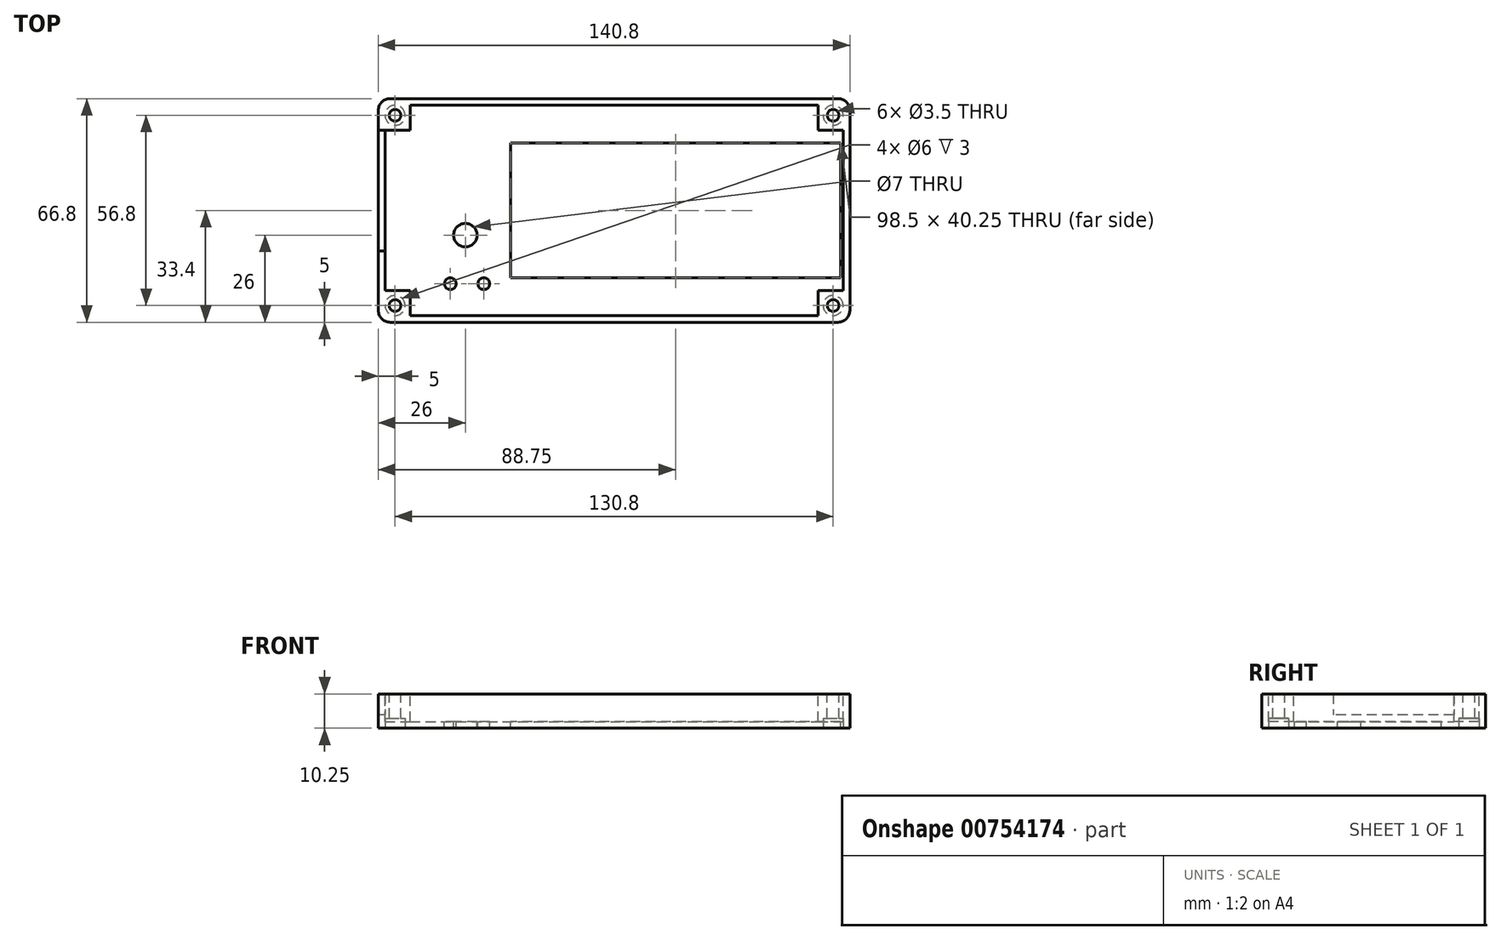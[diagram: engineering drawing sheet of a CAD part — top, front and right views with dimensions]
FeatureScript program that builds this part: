
annotation { "Feature Type Name" : "Feature", "Feature Type Description" : "" }
export const myFeature = defineFeature(function(context is Context, id is Id, definition is map)
    precondition{}
    {
        {
            var Q0;
            Q0=qCreatedBy(makeId("Top.planeOp"),FACE);
            var sketch = newSketch(context, id + "F0", { "sketchPlane" : qUnion([Q0])});
            skLineSegment(sketch, "E0.bottom", {"start": v(0, 0) * mm, "end": v(140.8, 0) * mm});
            skLineSegment(sketch, "E0.top", {"start": v(0, 66.8) * mm, "end": v(140.8, 66.8) * mm});
            skLineSegment(sketch, "E0.left", {"start": v(0, 0) * mm, "end": v(0, 66.8) * mm});
            skLineSegment(sketch, "E0.right", {"start": v(140.8, 0) * mm, "end": v(140.8, 66.8) * mm});
            skLineSegment(sketch, "E1.0", {"start": v(2, 64.8) * mm, "end": v(138.8, 64.8) * mm});
            skLineSegment(sketch, "E1.1", {"start": v(2, 2) * mm, "end": v(2, 64.8) * mm});
            skLineSegment(sketch, "E1.2", {"start": v(2, 2) * mm, "end": v(138.8, 2) * mm});
            skLineSegment(sketch, "E1.3", {"start": v(138.8, 2) * mm, "end": v(138.8, 64.8) * mm});
            skLineSegment(sketch, "E2", {"start": v(2, 57.3) * mm, "end": v(138.8, 57.3) * mm});
            skLineSegment(sketch, "E3", {"start": v(2, 9.5) * mm, "end": v(138.8, 9.5) * mm});
            skLineSegment(sketch, "E4", {"start": v(131.3, 64.8) * mm, "end": v(131.3, 2) * mm});
            skLineSegment(sketch, "E5", {"start": v(9.5, 64.8) * mm, "end": v(9.5, 2) * mm});
            skLineSegment(sketch, "E6.bottom", {"start": v(138, 53.53) * mm, "end": v(39.5, 53.53) * mm});
            skLineSegment(sketch, "E6.top", {"start": v(138, 13.28) * mm, "end": v(39.5, 13.28) * mm});
            skLineSegment(sketch, "E6.left", {"start": v(138, 53.53) * mm, "end": v(138, 13.28) * mm});
            skLineSegment(sketch, "E6.right", {"start": v(39.5, 53.53) * mm, "end": v(39.5, 13.28) * mm});
            skLineSegment(sketch, "E7", {"start": v(0, 33.4) * mm, "end": v(140.8, 33.4) * mm, "construction": true});
            skLineSegment(sketch, "E8", {"start": v(5, 83.26) * mm, "end": v(5, -9.4) * mm, "construction": true});
            skLineSegment(sketch, "E9", {"start": v(135.8, 85.49) * mm, "end": v(135.8, -7.35) * mm, "construction": true});
            skLineSegment(sketch, "E10", {"start": v(-12.85, 61.8) * mm, "end": v(160.3, 61.8) * mm, "construction": true});
            skLineSegment(sketch, "E11", {"start": v(-16.1, 5) * mm, "end": v(171.8, 5) * mm, "construction": true});
            skCircle(sketch, "E12", {"center": v(5, 61.8) * mm, "radius": 1.75 * mm});
            skCircle(sketch, "E13", {"center": v(135.8, 61.8) * mm, "radius": 1.75 * mm});
            skCircle(sketch, "E14", {"center": v(135.8, 5) * mm, "radius": 1.75 * mm});
            skCircle(sketch, "E15", {"center": v(5, 5) * mm, "radius": 1.75 * mm});
            skCircle(sketch, "E16", {"center": v(26, 26) * mm, "radius": 3.5 * mm});
            skCircle(sketch, "E17", {"center": v(21.5, 11.5) * mm, "radius": 1.75 * mm});
            skCircle(sketch, "E18", {"center": v(31.5, 11.5) * mm, "radius": 1.75 * mm});
            skSolve(sketch);
        }
        {
            var Q0;
            Q0 = qSketchRegion(id + "F0", true);
            var Q1;
            {var subQ5=sQuery(id+"F0.wireOp",EDGE,"E6.right");Q1=makeQuery(id+"F0.imprint","IMPRINT",FACE,{"disambiguationData":[TD([[makeQuery(id+"F0.imprint","IMPRINT",EDGE,{"derivedFrom":subQ5}),-1.0]])]});}
            var Q2;
            {var subQ0=sQuery(id+"F0.wireOp",EDGE,"E2");var subQ1=sQuery(id+"F0.wireOp",EDGE,"E1.1");var subQ2=makeQuery(id+"F0.imprint","INTERSECT",VERTEX,{"derivedFrom":[subQ1,subQ0]});Q2=makeQuery(id+"F0.imprint","IMPRINT",FACE,{"disambiguationData":[TD([[makeQuery(id+"F0.imprint","IMPRINT",EDGE,{"disambiguationData":[TD([[subQ2,1.0]])],"derivedFrom":subQ1}),-1.0]])]});}
            var Q3;
            Q3=makeQuery(id+"F0.imprint","IMPRINT",FACE,{"disambiguationData":[TD([[makeQuery(id+"F0.imprint","IMPRINT",EDGE,{"derivedFrom":sQuery(id+"F0.wireOp",EDGE,"E12")}),-1.0]])]});
            var Q4;
            {var subQ0=sQuery(id+"F0.wireOp",EDGE,"E4");var subQ1=sQuery(id+"F0.wireOp",EDGE,"E1.0");var subQ2=makeQuery(id+"F0.imprint","INTERSECT",VERTEX,{"derivedFrom":[subQ1,subQ0]});Q4=makeQuery(id+"F0.imprint","IMPRINT",FACE,{"disambiguationData":[TD([[makeQuery(id+"F0.imprint","IMPRINT",EDGE,{"disambiguationData":[TD([[subQ2,1.0]])],"derivedFrom":subQ1}),-1.0]])]});}
            var Q5;
            Q5=makeQuery(id+"F0.imprint","IMPRINT",FACE,{"disambiguationData":[TD([[makeQuery(id+"F0.imprint","IMPRINT",EDGE,{"derivedFrom":sQuery(id+"F0.wireOp",EDGE,"E13")}),-1.0]])]});
            var Q6;
            {var subQ5=sQuery(id+"F0.wireOp",EDGE,"E6.left");Q6=makeQuery(id+"F0.imprint","IMPRINT",FACE,{"disambiguationData":[TD([[makeQuery(id+"F0.imprint","IMPRINT",EDGE,{"derivedFrom":subQ5}),1.0]])]});}
            var Q7;
            Q7=makeQuery(id+"F0.imprint","IMPRINT",FACE,{"disambiguationData":[TD([[makeQuery(id+"F0.imprint","IMPRINT",EDGE,{"derivedFrom":sQuery(id+"F0.wireOp",EDGE,"E14")}),-1.0]])]});
            var Q8;
            {var subQ0=sQuery(id+"F0.wireOp",EDGE,"E4");var subQ1=sQuery(id+"F0.wireOp",EDGE,"E1.2");var subQ2=makeQuery(id+"F0.imprint","INTERSECT",VERTEX,{"derivedFrom":[subQ1,subQ0]});Q8=makeQuery(id+"F0.imprint","IMPRINT",FACE,{"disambiguationData":[TD([[makeQuery(id+"F0.imprint","IMPRINT",EDGE,{"disambiguationData":[TD([[subQ2,1.0]])],"derivedFrom":subQ1}),1.0]])]});}
            var Q9;
            Q9=makeQuery(id+"F0.imprint","IMPRINT",FACE,{"disambiguationData":[TD([[makeQuery(id+"F0.imprint","IMPRINT",EDGE,{"derivedFrom":sQuery(id+"F0.wireOp",EDGE,"E15")}),-1.0]])]});
            extrude(context, id + "F1", {"entities" : qUnion([Q0, Q1, Q2, Q3, Q4, Q5, Q6, Q7, Q8, Q9]), "oppositeDirection" : true, "depth" : (6.5 + 3.75) * mm, "offsetDistance" : 25 * mm});
        }
        {
            var Q0;
            {var subQ0=sQuery(id+"F0.wireOp",EDGE,"E4");var subQ1=sQuery(id+"F0.wireOp",EDGE,"E1.0");var subQ2=makeQuery(id+"F0.imprint","INTERSECT",VERTEX,{"derivedFrom":[subQ1,subQ0]});Q0=makeQuery(id+"F0.imprint","IMPRINT",FACE,{"disambiguationData":[TD([[makeQuery(id+"F0.imprint","IMPRINT",EDGE,{"disambiguationData":[TD([[subQ2,1.0]])],"derivedFrom":subQ1}),-1.0]])]});}
            var Q1;
            {var subQ5=sQuery(id+"F0.wireOp",EDGE,"E6.right");Q1=makeQuery(id+"F0.imprint","IMPRINT",FACE,{"disambiguationData":[TD([[makeQuery(id+"F0.imprint","IMPRINT",EDGE,{"derivedFrom":subQ5}),-1.0]])]});}
            var Q2;
            {var subQ0=sQuery(id+"F0.wireOp",EDGE,"E4");var subQ1=sQuery(id+"F0.wireOp",EDGE,"E1.2");var subQ2=makeQuery(id+"F0.imprint","INTERSECT",VERTEX,{"derivedFrom":[subQ1,subQ0]});Q2=makeQuery(id+"F0.imprint","IMPRINT",FACE,{"disambiguationData":[TD([[makeQuery(id+"F0.imprint","IMPRINT",EDGE,{"disambiguationData":[TD([[subQ2,1.0]])],"derivedFrom":subQ1}),1.0]])]});}
            var Q3;
            {var subQ0=sQuery(id+"F0.wireOp",EDGE,"E2");var subQ1=sQuery(id+"F0.wireOp",EDGE,"E1.1");var subQ2=makeQuery(id+"F0.imprint","INTERSECT",VERTEX,{"derivedFrom":[subQ1,subQ0]});Q3=makeQuery(id+"F0.imprint","IMPRINT",FACE,{"disambiguationData":[TD([[makeQuery(id+"F0.imprint","IMPRINT",EDGE,{"disambiguationData":[TD([[subQ2,1.0]])],"derivedFrom":subQ1}),-1.0]])]});}
            var Q4;
            {var subQ5=sQuery(id+"F0.wireOp",EDGE,"E6.left");Q4=makeQuery(id+"F0.imprint","IMPRINT",FACE,{"disambiguationData":[TD([[makeQuery(id+"F0.imprint","IMPRINT",EDGE,{"derivedFrom":subQ5}),1.0]])]});}
            extrude(context, id + "F2", {"entities" : qUnion([Q0, Q1, Q2, Q3, Q4]), "operationType" : NewBodyOperationType.REMOVE, "oppositeDirection" : true, "depth" : 8.25 * mm, "offsetDistance" : 25 * mm});
        }
        {
            var Q0;
            Q0=makeQuery(id+"F1.opExtrude","SWEPT_EDGE",EDGE,{"disambiguationData":[OSD([sQuery(id+"F0.wireOp",EDGE,"E0.top"),sQuery(id+"F0.wireOp",EDGE,"E0.right")])]});
            var Q1;
            Q1=makeQuery(id+"F1.opExtrude","SWEPT_EDGE",EDGE,{"disambiguationData":[OSD([sQuery(id+"F0.wireOp",EDGE,"E0.top"),sQuery(id+"F0.wireOp",EDGE,"E0.left")])]});
            var Q2;
            Q2=makeQuery(id+"F1.opExtrude","SWEPT_EDGE",EDGE,{"disambiguationData":[OSD([sQuery(id+"F0.wireOp",EDGE,"E0.bottom"),sQuery(id+"F0.wireOp",EDGE,"E0.left")])]});
            var Q3;
            Q3=makeQuery(id+"F1.opExtrude","SWEPT_EDGE",EDGE,{"disambiguationData":[OSD([sQuery(id+"F0.wireOp",EDGE,"E0.bottom"),sQuery(id+"F0.wireOp",EDGE,"E0.right")])]});
            fillet(context, id + "F3", {"entities" : qUnion([Q0, Q1, Q2, Q3]), "radius" : 3.5 * mm, "tangentPropagation" : true, "allowEdgeOverflow" : false});
        }
        {
            var Q0;
            Q0=makeQuery(id+"F1.opExtrude","CAP_FACE",FACE,{"disambiguationData":[OSD([sQuery(id+"F0.wireOp",EDGE,"E0.bottom"),sQuery(id+"F0.wireOp",EDGE,"E0.top"),sQuery(id+"F0.wireOp",EDGE,"E0.left"),sQuery(id+"F0.wireOp",EDGE,"E0.right"),sQuery(id+"F0.wireOp",EDGE,"E6.bottom"),sQuery(id+"F0.wireOp",EDGE,"E6.top"),sQuery(id+"F0.wireOp",EDGE,"E6.left"),sQuery(id+"F0.wireOp",EDGE,"E6.right"),sQuery(id+"F0.wireOp",EDGE,"E12"),sQuery(id+"F0.wireOp",EDGE,"E13"),sQuery(id+"F0.wireOp",EDGE,"E14"),sQuery(id+"F0.wireOp",EDGE,"E15"),sQuery(id+"F0.wireOp",EDGE,"E16"),sQuery(id+"F0.wireOp",EDGE,"E17"),sQuery(id+"F0.wireOp",EDGE,"E18")])],"isStart":false});
            var sketch = newSketch(context, id + "F4", { "sketchPlane" : qUnion([Q0])});
            skCircle(sketch, "E19.0", {"center": v(5, -5) * mm, "radius": 3 * mm});
            skCircle(sketch, "E20.0", {"center": v(135.8, -5) * mm, "radius": 3 * mm});
            skCircle(sketch, "E21.0", {"center": v(135.8, -61.8) * mm, "radius": 3 * mm});
            skCircle(sketch, "E22.0", {"center": v(5, -61.8) * mm, "radius": 3 * mm});
            skSolve(sketch);
        }
        {
            var Q0;
            Q0 = qSketchRegion(id + "F4", true);
            extrude(context, id + "F5", {"entities" : qUnion([Q0]), "operationType" : NewBodyOperationType.REMOVE, "oppositeDirection" : true, "depth" : 3 * mm, "offsetDistance" : 25 * mm});
        }
        {
            var Q0;
            Q0=makeQuery(id+"F1.opExtrude","SWEPT_FACE",FACE,{"disambiguationData":[OSD([sQuery(id+"F0.wireOp",EDGE,"E0.left")])]});
            var sketch = newSketch(context, id + "F6", { "sketchPlane" : qUnion([Q0])});
            skLineSegment(sketch, "E23.bottom", {"start": v(-57.3, 0) * mm, "end": v(-21.3, 0) * mm});
            skLineSegment(sketch, "E23.top", {"start": v(-57.3, -6.25) * mm, "end": v(-21.3, -6.25) * mm});
            skLineSegment(sketch, "E23.left", {"start": v(-57.3, 0) * mm, "end": v(-57.3, -6.25) * mm});
            skLineSegment(sketch, "E23.right", {"start": v(-21.3, 0) * mm, "end": v(-21.3, -6.25) * mm});
            skSolve(sketch);
        }
        {
            var Q0;
            Q0 = qSketchRegion(id + "F6", true);
            extrude(context, id + "F7", {"entities" : qUnion([Q0]), "operationType" : NewBodyOperationType.REMOVE, "oppositeDirection" : true, "depth" : 2 * mm, "offsetDistance" : 25 * mm});
        }
    });
